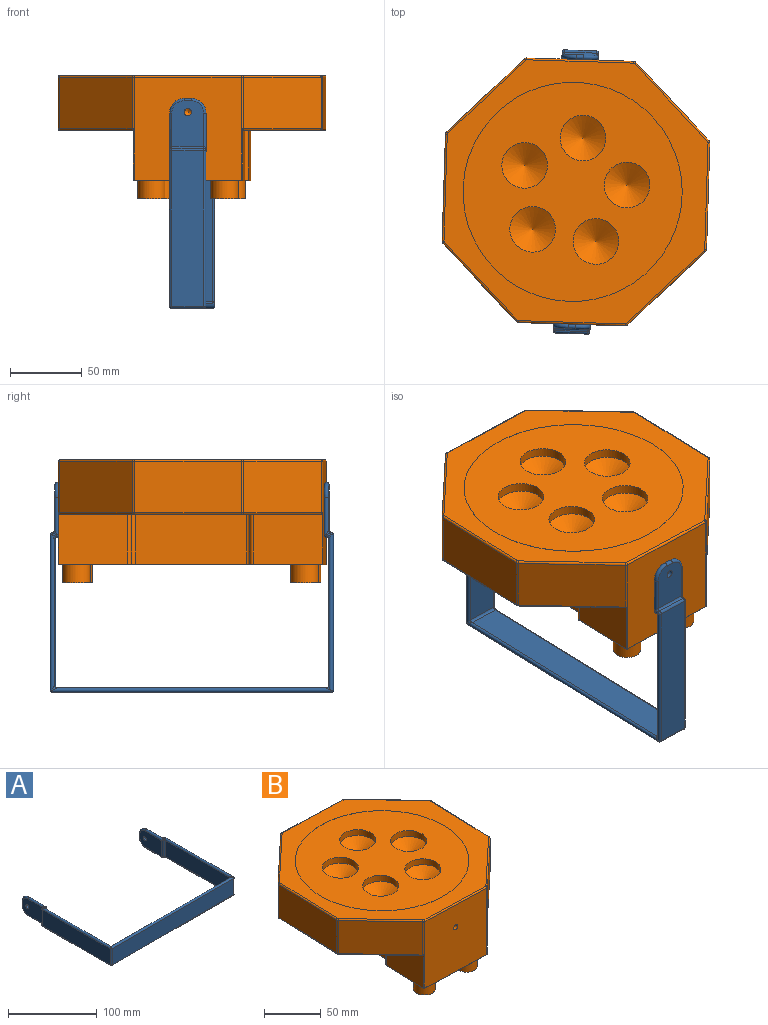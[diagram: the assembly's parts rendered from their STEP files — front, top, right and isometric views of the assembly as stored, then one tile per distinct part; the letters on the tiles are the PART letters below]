
ASSEMBLY  parts=2 mates=1
PART A: 68 faces, bbox 196.9x146.9x27.1 mm
  f0: plane 101.6x22.23mm, normal (-1,0,0), area 2258.1mm2, adj f12,f24,f33,f46
  f1: plane 193.68x22.23mm, normal (0,-1,0), area 4304.4mm2, adj f13,f23,f54,f66
  f2: plane 107.95x22.23mm, normal (1,0,0), area 2399.2mm2, adj f12,f24,f40,f54
  f3: plane 187.33x22.23mm, normal (0,1,0), area 4163.3mm2, adj f13,f23,f46,f63
  f4: plane 107.95x22.23mm, normal (-1,0,0), area 2399.2mm2, adj f14,f22,f60,f66
  f5: plane 101.6x22.23mm, normal (1,0,0), area 2258.1mm2, adj f14,f22,f52,f63
  f6: plane 34.93x22.23mm, normal (-1,0,0), area 724.2mm2, adj f11,f26,f27,f28,f29,f30,f35
  f7: plane 31.75x22.23mm, normal (1,0,0), area 653.6mm2, adj f11,f26,f27,f28,f29,f30,f37
  f8: plane 34.93x22.23mm, normal (1,0,0), area 724.2mm2, adj f10,f16,f17,f18,f19,f20,f50
  f9: plane 31.75x22.23mm, normal (-1,0,0), area 653.6mm2, adj f10,f16,f17,f18,f19,f20,f59
  f10: cylinder r=2.55mm len=5.11mm, axis (1,0,0), area 50.9mm2, adj f8,f9
  f11: cylinder r=2.55mm len=5.11mm, axis (-1,0,0), area 50.9mm2, adj f6,f7
  f12: cylinder r=1.59mm len=107.95mm, axis (0,1,0), area 528.3mm2, adj f0,f2,f39,f42,f45,f53
  f13: cylinder r=1.59mm len=193.68mm, axis (1,0,0), area 955.8mm2, adj f1,f3,f45,f53,f64,f67
  f14: cylinder r=1.59mm len=107.95mm, axis (0,-1,0), area 528.3mm2, adj f4,f5,f51,f58,f64,f67
  f15: cylinder r=1.59mm len=3.18mm, axis (1,0,0), area 5.8mm2, adj f48,f51,f56,f58
  f16: cylinder r=1.59mm len=26.35mm, axis (0,1,0), area 126.4mm2, adj f8,f9,f17,f48,f56
  f17: torus R=8.57mm, axis (-1,0,0), area 75.1mm2, adj f8,f9,f16,f18
  f18: cylinder r=1.59mm len=5.08mm, axis (0,0,-1), area 25.3mm2, adj f8,f9,f17,f19
  f19: torus R=8.57mm, axis (-1,0,0), area 75.1mm2, adj f8,f9,f18,f20
  f20: cylinder r=1.59mm len=26.35mm, axis (0,-1,0), area 126.4mm2, adj f8,f9,f19,f47,f57
  f21: cylinder r=1.59mm len=3.18mm, axis (-1,0,0), area 5.8mm2, adj f47,f49,f57,f61
  f22: cylinder r=1.59mm len=107.95mm, axis (0,1,0), area 528.3mm2, adj f4,f5,f49,f61,f62,f65
  f23: cylinder r=1.59mm len=193.68mm, axis (-1,0,0), area 955.8mm2, adj f1,f3,f44,f55,f62,f65
  f24: cylinder r=1.59mm len=107.95mm, axis (0,-1,0), area 528.3mm2, adj f0,f2,f31,f36,f44,f55
  f25: cylinder r=1.59mm len=3.18mm, axis (-1,0,0), area 5.8mm2, adj f31,f32,f34,f36
  f26: cylinder r=1.59mm len=26.35mm, axis (0,1,0), area 126.4mm2, adj f6,f7,f27,f32,f34
  f27: torus R=8.57mm, axis (-1,0,0), area 75.1mm2, adj f6,f7,f26,f28
  f28: cylinder r=1.59mm len=5.08mm, axis (0,0,1), area 25.3mm2, adj f6,f7,f27,f29
  f29: torus R=8.57mm, axis (-1,0,0), area 75.1mm2, adj f6,f7,f28,f30
  f30: cylinder r=1.59mm len=26.35mm, axis (0,-1,0), area 126.4mm2, adj f6,f7,f29,f38,f43
  f31: bspline ~3.18x3.18mm, area 4.8mm2, adj f24,f25,f33
  f32: sphere r=1.59mm, area 4mm2, adj f25,f26,f35
  f33: cylinder r=1.59mm len=22.23mm, axis (0,0,1), area 55.4mm2, adj f0,f31,f35,f39
  f34: bspline ~3.18x3.18mm, area 4.8mm2, adj f25,f26,f37
  f35: cylinder r=1.59mm len=22.23mm, axis (0,0,-1), area 55.4mm2, adj f6,f32,f33,f38
  f36: sphere r=1.59mm, area 4mm2, adj f24,f25,f40
  f37: cylinder r=1.59mm len=22.23mm, axis (0,0,-1), area 55.4mm2, adj f7,f34,f40,f43
  f38: sphere r=1.59mm, area 4mm2, adj f30,f35,f41
  f39: bspline ~3.18x3.18mm, area 4.8mm2, adj f12,f33,f41
  f40: cylinder r=1.59mm len=22.23mm, axis (0,0,1), area 55.4mm2, adj f2,f36,f37,f42
  f41: cylinder r=1.59mm len=3.18mm, axis (-1,0,0), area 5.8mm2, adj f38,f39,f42,f43
  f42: sphere r=1.59mm, area 4mm2, adj f12,f40,f41
  f43: bspline ~3.18x3.18mm, area 4.8mm2, adj f30,f37,f41
  f44: bspline ~3.18x3.18mm, area 4.8mm2, adj f23,f24,f46
  f45: bspline ~3.18x3.18mm, area 4.8mm2, adj f12,f13,f46
  f46: cylinder r=1.59mm len=22.23mm, axis (0,0,-1), area 55.4mm2, adj f0,f3,f44,f45
  f47: sphere r=1.59mm, area 4mm2, adj f20,f21,f50
  f48: sphere r=1.59mm, area 4mm2, adj f15,f16,f50
  f49: bspline ~3.18x3.18mm, area 4.8mm2, adj f21,f22,f52
  f50: cylinder r=1.59mm len=22.23mm, axis (0,0,1), area 55.4mm2, adj f8,f47,f48,f52
  f51: bspline ~3.18x3.18mm, area 4.8mm2, adj f14,f15,f52
  f52: cylinder r=1.59mm len=22.23mm, axis (0,0,-1), area 55.4mm2, adj f5,f49,f50,f51
  f53: sphere r=1.59mm, area 4mm2, adj f12,f13,f54
  f54: cylinder r=1.59mm len=22.23mm, axis (0,0,1), area 55.4mm2, adj f1,f2,f53,f55
  f55: sphere r=1.59mm, area 4mm2, adj f23,f24,f54
  f56: bspline ~3.18x3.18mm, area 4.8mm2, adj f15,f16,f59
  f57: bspline ~3.18x3.18mm, area 4.8mm2, adj f20,f21,f59
  f58: sphere r=1.59mm, area 4mm2, adj f14,f15,f60
  f59: cylinder r=1.59mm len=22.23mm, axis (0,0,1), area 55.4mm2, adj f9,f56,f57,f60
  f60: cylinder r=1.59mm len=22.23mm, axis (0,0,-1), area 55.4mm2, adj f4,f58,f59,f61
  f61: sphere r=1.59mm, area 4mm2, adj f21,f22,f60
  f62: bspline ~3.18x3.18mm, area 4.8mm2, adj f22,f23,f63
  f63: cylinder r=1.59mm len=22.23mm, axis (0,0,1), area 55.4mm2, adj f3,f5,f62,f64
  f64: bspline ~3.18x3.18mm, area 4.8mm2, adj f13,f14,f63
  f65: sphere r=1.59mm, area 4mm2, adj f22,f23,f66
  f66: cylinder r=1.59mm len=22.23mm, axis (0,0,-1), area 55.4mm2, adj f1,f4,f65,f67
  f67: sphere r=1.59mm, area 4mm2, adj f13,f14,f66
PART B: 116 faces, bbox 186.6x186.6x85.7 mm
  f0: cylinder r=9.53mm len=19.05mm, axis (0,0,1), area 760.1mm2, adj f1,f8
  f1: plane 19.05x19.05mm, normal (0,0,-1), area 285mm2, adj f0
  f2: cylinder r=9.53mm len=19.05mm, axis (0,0,1), area 760.1mm2, adj f3,f8
  f3: plane 19.05x19.05mm, normal (0,0,-1), area 285mm2, adj f2
  f4: cylinder r=9.53mm len=19.05mm, axis (0,0,1), area 760.1mm2, adj f5,f8
  f5: plane 19.05x19.05mm, normal (0,0,-1), area 285mm2, adj f4
  f6: plane 48.04x35.94mm, normal (1,-0.03,0), area 1666.6mm2, adj f9,f45,f73,f74,f87,f96
  f7: plane 48.04x35.94mm, normal (-1,0.03,0), area 1666.6mm2, adj f27,f49,f80,f81,f88,f107
  f8: plane 185.67x81.35mm, normal (0,0,-1), area 11696.1mm2, adj f0,f2,f4,f90,f91,f92,f93,f94
  f9: plane 180.28x61.29mm, normal (0,0,-1), area 7244.4mm2, adj f6,f32,f37,f38,f39,f69,f70,f71
  f10: cone r=0mm half-angle=59deg, axis (0,0,1), area 923.7mm2, adj f11
  f11: cylinder r=15.88mm len=31.75mm, axis (0,0,1), area 633.4mm2, adj f10,f29
  f12: cone r=0mm half-angle=59deg, axis (0,0,1), area 923.7mm2, adj f13
  f13: cylinder r=15.88mm len=31.75mm, axis (0,0,1), area 633.4mm2, adj f12,f29
  f14: cone r=0mm half-angle=59deg, axis (0,0,1), area 923.7mm2, adj f15
  f15: cylinder r=15.88mm len=31.75mm, axis (0,0,1), area 633.4mm2, adj f14,f29
  f16: cone r=0mm half-angle=59deg, axis (0,0,1), area 923.7mm2, adj f17
  f17: cylinder r=15.88mm len=31.75mm, axis (0,0,1), area 633.4mm2, adj f16,f29
  f18: plane 74.06x35.56mm, normal (1,-0.03,0), area 2634.8mm2, adj f44,f51,f63,f71
  f19: plane 54x50.74mm, normal (0.73,0.68,0), area 2634.8mm2, adj f44,f45,f67,f73
  f20: plane 74.06x71.5mm, normal (0.03,1,0), area 5277.5mm2, adj f41,f45,f46,f64,f100
  f21: plane 54x50.74mm, normal (-0.68,0.73,0), area 2634.8mm2, adj f46,f47,f60,f76
  f22: plane 74.06x35.56mm, normal (-1,0.03,0), area 2634.8mm2, adj f47,f48,f56,f78
  f23: plane 54x50.74mm, normal (-0.73,-0.68,0), area 2634.8mm2, adj f48,f49,f52,f80
  f24: plane 74.06x71.5mm, normal (-0.03,-1,0), area 5277.5mm2, adj f43,f49,f50,f55,f103
  f25: plane 54x50.74mm, normal (0.68,-0.73,0), area 2634.8mm2, adj f50,f51,f59,f69
  f26: plane 183.64x183.64mm, normal (0,0,1), area 9025.4mm2, adj f28,f52,f53,f54,f55,f56,f57,f58
  f27: plane 180.28x61.29mm, normal (0,0,-1), area 7244.2mm2, adj f7,f33,f34,f35,f36,f76,f77,f78
  f28: cylinder r=76.2mm len=152.4mm, axis (0,0,1), area 12.2mm2, adj f26,f29
  f29: plane 152.4x152.4mm, normal (0,0,1), area 14282.8mm2, adj f11,f13,f15,f17,f28,f31
  f30: cone r=0mm half-angle=59deg, axis (0,0,1), area 923.7mm2, adj f31
  f31: cylinder r=15.88mm len=31.75mm, axis (0,0,1), area 633.4mm2, adj f29,f30
  f32: plane 48.01x35.94mm, normal (1,-0.03,0), area 1665.7mm2, adj f9,f50,f68,f69,f84,f99
  f33: plane 48.04x35.94mm, normal (-1,0.03,0), area 1666.6mm2, adj f27,f46,f75,f76,f82,f104
  f34: plane 34.67x1.27mm, normal (0.03,1,0), area 44mm2, adj f27,f88,f89,f111
  f35: plane 34.67x1.27mm, normal (-0.03,-1,0), area 44mm2, adj f27,f82,f83,f108
  f36: plane 77.2x34.67mm, normal (-1,0.03,0), area 2677.8mm2, adj f27,f83,f89,f112
  f37: plane 34.67x1.27mm, normal (0.03,1,0), area 44mm2, adj f9,f84,f85,f95
  f38: plane 77.22x34.67mm, normal (1,-0.03,0), area 2678.6mm2, adj f9,f85,f86,f91
  f39: plane 34.67x1.27mm, normal (-0.03,-1,0), area 44mm2, adj f9,f86,f87,f92
  f40: cone r=0mm half-angle=59deg, axis (0.03,1,0), area 23.9mm2, adj f41
  f41: cylinder r=2.55mm len=6.51mm, axis (0.03,1,0), area 101.8mm2, adj f20,f40
  f42: cone r=0mm half-angle=59deg, axis (-0.03,-1,0), area 23.9mm2, adj f43
  f43: cylinder r=2.55mm len=6.51mm, axis (-0.03,-1,0), area 101.8mm2, adj f24,f42
  f44: cylinder r=2.54mm len=35.56mm, axis (0,0,-1), area 70.9mm2, adj f18,f19,f65,f72
  f45: cylinder r=2.54mm len=71.5mm, axis (0,0,-1), area 109.9mm2, adj f6,f19,f20,f66,f74,f98
  f46: cylinder r=2.54mm len=71.5mm, axis (0,0,-1), area 109.9mm2, adj f20,f21,f33,f62,f75,f102
  f47: cylinder r=2.54mm len=35.56mm, axis (0,0,-1), area 70.9mm2, adj f21,f22,f58,f77
  f48: cylinder r=2.54mm len=35.56mm, axis (0,0,-1), area 70.9mm2, adj f22,f23,f54,f79
  f49: cylinder r=2.54mm len=71.5mm, axis (0,0,-1), area 109.9mm2, adj f7,f23,f24,f53,f81,f105
  f50: cylinder r=2.54mm len=71.5mm, axis (0,0,-1), area 109.9mm2, adj f24,f25,f32,f57,f68,f101
  f51: cylinder r=2.54mm len=35.56mm, axis (0,0,-1), area 70.9mm2, adj f18,f25,f61,f70
  f52: cylinder r=1.27mm len=54.87mm, axis (-0.68,0.73,0), area 147.8mm2, adj f23,f26,f53,f54
  f53: torus R=1.27mm, axis (0,0,1), area 3.3mm2, adj f26,f49,f52,f55
  f54: torus R=1.27mm, axis (0,0,1), area 3.3mm2, adj f26,f48,f52,f56
  f55: cylinder r=1.27mm len=74.1mm, axis (-1,0.03,0), area 147.8mm2, adj f24,f26,f53,f57
  f56: cylinder r=1.27mm len=74.1mm, axis (0.03,1,0), area 147.8mm2, adj f22,f26,f54,f58
  f57: torus R=1.27mm, axis (0,0,1), area 3.3mm2, adj f26,f50,f55,f59
  f58: torus R=1.27mm, axis (0,0,1), area 3.3mm2, adj f26,f47,f56,f60
  f59: cylinder r=1.27mm len=54.87mm, axis (-0.73,-0.68,0), area 147.8mm2, adj f25,f26,f57,f61
  f60: cylinder r=1.27mm len=54.87mm, axis (0.73,0.68,0), area 147.8mm2, adj f21,f26,f58,f62
  f61: torus R=1.27mm, axis (0,0,1), area 3.3mm2, adj f26,f51,f59,f63
  f62: torus R=1.27mm, axis (0,0,1), area 3.3mm2, adj f26,f46,f60,f64
  f63: cylinder r=1.27mm len=74.1mm, axis (-0.03,-1,0), area 147.8mm2, adj f18,f26,f61,f65
  f64: cylinder r=1.27mm len=74.1mm, axis (1,-0.03,0), area 147.8mm2, adj f20,f26,f62,f66
  f65: torus R=1.27mm, axis (0,0,1), area 3.3mm2, adj f26,f44,f63,f67
  f66: torus R=1.27mm, axis (0,0,1), area 3.3mm2, adj f26,f45,f64,f67
  f67: cylinder r=1.27mm len=54.87mm, axis (0.68,-0.73,0), area 147.8mm2, adj f19,f26,f65,f66
  f68: torus R=1.27mm, axis (0,0,1), area 1.1mm2, adj f32,f50,f69
  f69: cylinder r=1.27mm len=54.87mm, axis (0.73,0.68,0), area 147.8mm2, adj f9,f25,f32,f68,f70
  f70: torus R=1.27mm, axis (0,0,1), area 3.3mm2, adj f9,f51,f69,f71
  f71: cylinder r=1.27mm len=74.1mm, axis (0.03,1,0), area 147.8mm2, adj f9,f18,f70,f72
  f72: torus R=1.27mm, axis (0,0,1), area 3.3mm2, adj f9,f44,f71,f73
  f73: cylinder r=1.27mm len=54.87mm, axis (-0.68,0.73,0), area 147.8mm2, adj f6,f9,f19,f72,f74
  f74: torus R=1.27mm, axis (0,0,1), area 1.1mm2, adj f6,f45,f73
  f75: torus R=1.27mm, axis (0,0,1), area 1.1mm2, adj f33,f46,f76
  f76: cylinder r=1.27mm len=54.87mm, axis (-0.73,-0.68,0), area 147.8mm2, adj f21,f27,f33,f75,f77
  f77: torus R=1.27mm, axis (0,0,1), area 3.3mm2, adj f27,f47,f76,f78
  f78: cylinder r=1.27mm len=74.1mm, axis (-0.03,-1,0), area 147.8mm2, adj f22,f27,f77,f79
  f79: torus R=1.27mm, axis (0,0,1), area 3.3mm2, adj f27,f48,f78,f80
  f80: cylinder r=1.27mm len=54.87mm, axis (0.68,-0.73,0), area 147.8mm2, adj f7,f23,f27,f79,f81
  f81: torus R=1.27mm, axis (0,0,1), area 1.1mm2, adj f7,f49,f80
  f82: cylinder r=2.54mm len=34.67mm, axis (0,0,1), area 138.3mm2, adj f27,f33,f35,f106
  f83: cylinder r=2.54mm len=34.67mm, axis (0,0,1), area 138.3mm2, adj f27,f35,f36,f110
  f84: cylinder r=2.54mm len=34.67mm, axis (0,0,1), area 138.3mm2, adj f9,f32,f37,f97
  f85: cylinder r=2.54mm len=34.67mm, axis (0,0,1), area 138.3mm2, adj f9,f37,f38,f93
  f86: cylinder r=2.54mm len=34.67mm, axis (0,0,1), area 138.3mm2, adj f9,f38,f39,f90
  f87: cylinder r=2.54mm len=34.67mm, axis (0,0,1), area 138.3mm2, adj f6,f9,f39,f94
  f88: cylinder r=2.54mm len=34.67mm, axis (0,0,-1), area 138.3mm2, adj f7,f27,f34,f109
  f89: cylinder r=2.54mm len=34.67mm, axis (0,0,-1), area 138.3mm2, adj f27,f34,f36,f113
  f90: torus R=2.79mm, axis (0,0,-1), area 1.6mm2, adj f8,f86,f91,f92
  f91: cylinder r=0.25mm len=77.23mm, axis (-0.03,-1,0), area 30.8mm2, adj f8,f38,f90,f93
  f92: cylinder r=0.25mm len=1.28mm, axis (-1,0.03,0), area 0.5mm2, adj f8,f39,f90,f94
  f93: torus R=2.79mm, axis (0,0,-1), area 1.6mm2, adj f8,f85,f91,f95
  f94: torus R=2.29mm, axis (0,0,-1), area 1.5mm2, adj f8,f87,f92,f96
  f95: cylinder r=0.25mm len=1.28mm, axis (1,-0.03,0), area 0.5mm2, adj f8,f37,f93,f97
  f96: cylinder r=0.25mm len=48.04mm, axis (0.03,1,0), area 19.1mm2, adj f6,f8,f94,f98
  f97: torus R=2.29mm, axis (0,0,-1), area 1.5mm2, adj f8,f84,f95,f99
  f98: torus R=2.29mm, axis (0,0,-1), area 0.4mm2, adj f8,f45,f96,f100
  f99: cylinder r=0.25mm len=48.02mm, axis (0.03,1,0), area 19.1mm2, adj f8,f32,f97,f101
  f100: cylinder r=0.25mm len=74.07mm, axis (1,-0.03,0), area 29.6mm2, adj f8,f20,f98,f102
  f101: torus R=2.29mm, axis (0,0,-1), area 0.4mm2, adj f8,f50,f99,f103
  f102: torus R=2.29mm, axis (0,0,-1), area 0.4mm2, adj f8,f46,f100,f104
  f103: cylinder r=0.25mm len=74.07mm, axis (-1,0.03,0), area 29.6mm2, adj f8,f24,f101,f105
  f104: cylinder r=0.25mm len=48.04mm, axis (-0.03,-1,0), area 19.1mm2, adj f8,f33,f102,f106
  f105: torus R=2.29mm, axis (0,0,-1), area 0.4mm2, adj f8,f49,f103,f107
  f106: torus R=2.29mm, axis (0,0,-1), area 1.5mm2, adj f8,f82,f104,f108
  f107: cylinder r=0.25mm len=48.04mm, axis (-0.03,-1,0), area 19.1mm2, adj f7,f8,f105,f109
  f108: cylinder r=0.25mm len=1.28mm, axis (-1,0.03,0), area 0.5mm2, adj f8,f35,f106,f110
  f109: torus R=2.29mm, axis (0,0,-1), area 1.5mm2, adj f8,f88,f107,f111
  f110: torus R=2.79mm, axis (0,0,-1), area 1.6mm2, adj f8,f83,f108,f112
  f111: cylinder r=0.25mm len=1.28mm, axis (1,-0.03,0), area 0.5mm2, adj f8,f34,f109,f113
  f112: cylinder r=0.25mm len=77.2mm, axis (0.03,1,0), area 30.8mm2, adj f8,f36,f110,f113
  f113: torus R=2.79mm, axis (0,0,-1), area 1.6mm2, adj f8,f89,f111,f112
  f114: cylinder r=9.53mm len=19.05mm, axis (0,0,1), area 760.1mm2, adj f8,f115
  f115: plane 19.05x19.05mm, normal (0,0,-1), area 285mm2, adj f114
PLACE A rot(axis=(0.57,-0.58,-0.58),121deg) t=(-26.5,-25.4,-111.89)mm
PLACE B t=(-41.55,-25.1,10.34)mm
MATE planar A.f6 <-> B.f24  axis (0.03,1,0) through (-42.06,-117.04,12.57)mm
